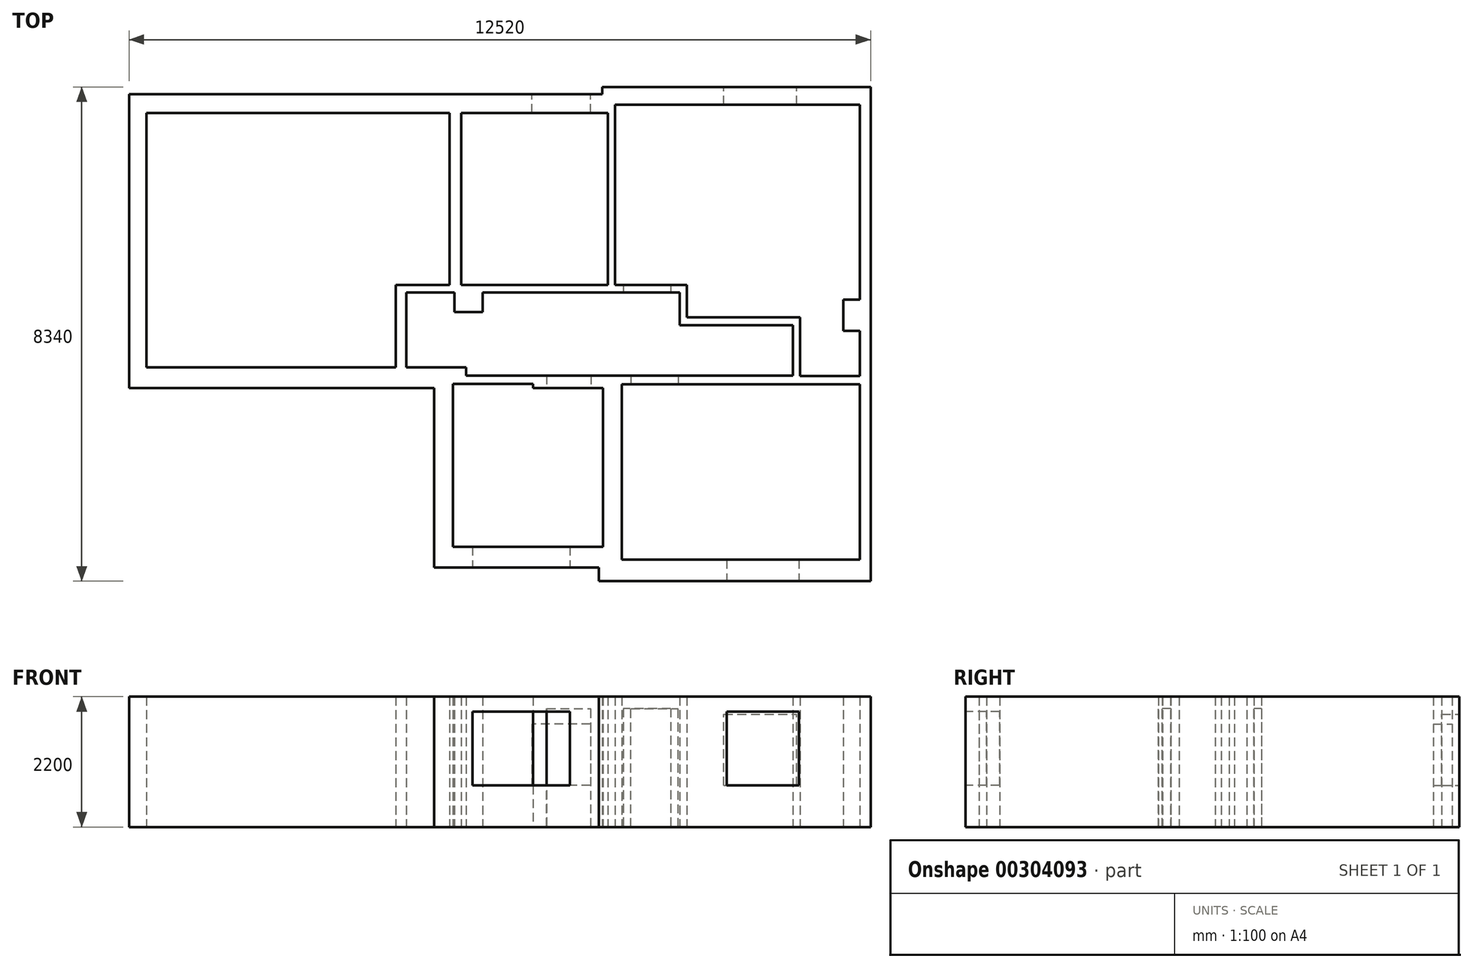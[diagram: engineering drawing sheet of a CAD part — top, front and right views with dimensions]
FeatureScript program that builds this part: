
annotation { "Feature Type Name" : "Feature", "Feature Type Description" : "" }
export const myFeature = defineFeature(function(context is Context, id is Id, definition is map)
    precondition{}
    {
        {
            var Q0;
            Q0=qCreatedBy(makeId("Top.planeOp"),FACE);
            var sketch = newSketch(context, id + "F0", { "sketchPlane" : qUnion([Q0])});
            skLineSegment(sketch, "E0", {"start": v(1913.2, -215.96) * mm, "end": v(-3236.8, -215.96) * mm});
            skLineSegment(sketch, "E1", {"start": v(-3236.8, 4744.04) * mm, "end": v(-3236.8, -215.96) * mm});
            skLineSegment(sketch, "E2", {"start": v(1913.2, -3245.96) * mm, "end": v(4693.2, -3245.96) * mm});
            skLineSegment(sketch, "E3", {"start": v(4763.2, -2895.96) * mm, "end": v(2233.2, -2895.96) * mm});
            skLineSegment(sketch, "E4", {"start": v(4693.2, -3245.96) * mm, "end": v(4693.2, -3475.96) * mm});
            skLineSegment(sketch, "E5", {"start": v(4693.2, -3475.96) * mm, "end": v(9283.2, -3475.96) * mm});
            skLineSegment(sketch, "E6", {"start": v(9283.2, -3475.96) * mm, "end": v(9283.2, 4864.04) * mm});
            skLineSegment(sketch, "E7", {"start": v(9283.2, 4864.04) * mm, "end": v(4753.2, 4864.04) * mm});
            skLineSegment(sketch, "E8", {"start": v(4968.2, 4564.04) * mm, "end": v(9103.2, 4564.04) * mm});
            skLineSegment(sketch, "E9", {"start": v(9103.2, -3115.96) * mm, "end": v(5083.2, -3115.96) * mm});
            skLineSegment(sketch, "E10", {"start": v(9103.2, -155.96) * mm, "end": v(5083.2, -155.96) * mm});
            skLineSegment(sketch, "E11.bottom", {"start": v(9103.2, 1274.04) * mm, "end": v(8823.2, 1274.04) * mm});
            skLineSegment(sketch, "E11.top", {"start": v(9103.2, 744.04) * mm, "end": v(8823.2, 744.04) * mm});
            skLineSegment(sketch, "E11.right", {"start": v(8823.2, 1274.04) * mm, "end": v(8823.2, 744.04) * mm});
            skLineSegment(sketch, "E12", {"start": v(2173.2, 4424.04) * mm, "end": v(2173.2, 1524.04) * mm});
            skLineSegment(sketch, "E13", {"start": v(2173.2, 1524.04) * mm, "end": v(1263.2, 1524.04) * mm});
            skLineSegment(sketch, "E14", {"start": v(6058.2, 1394.04) * mm, "end": v(6058.2, 844.04) * mm});
            skLineSegment(sketch, "E15", {"start": v(6058.2, 844.04) * mm, "end": v(7968.2, 844.04) * mm});
            skLineSegment(sketch, "E16", {"start": v(7968.2, 844.04) * mm, "end": v(7968.2, -5.96) * mm});
            skLineSegment(sketch, "E17", {"start": v(8088.2, -15.96) * mm, "end": v(8088.2, 974.04) * mm});
            skLineSegment(sketch, "E18", {"start": v(8088.2, 974.04) * mm, "end": v(6178.2, 974.04) * mm});
            skLineSegment(sketch, "E19", {"start": v(6178.2, 974.04) * mm, "end": v(6178.2, 1524.04) * mm});
            skLineSegment(sketch, "E20", {"start": v(6178.2, 1524.04) * mm, "end": v(4968.2, 1524.04) * mm});
            skLineSegment(sketch, "E21", {"start": v(4968.2, 1524.04) * mm, "end": v(4968.2, 4564.04) * mm});
            skLineSegment(sketch, "E22", {"start": v(4848.2, 1524.04) * mm, "end": v(2368.2, 1524.04) * mm});
            skLineSegment(sketch, "E23", {"start": v(2368.2, 1524.04) * mm, "end": v(2368.2, 4424.04) * mm});
            skLineSegment(sketch, "E24", {"start": v(2253.2, 1394.04) * mm, "end": v(2253.2, 1064.04) * mm});
            skLineSegment(sketch, "E25", {"start": v(2253.2, 1064.04) * mm, "end": v(2733.2, 1064.04) * mm});
            skLineSegment(sketch, "E26", {"start": v(2733.2, 1064.04) * mm, "end": v(2733.2, 1394.04) * mm});
            skLineSegment(sketch, "E27", {"start": v(4848.2, 4424.04) * mm, "end": v(4848.2, 1524.04) * mm});
            skLineSegment(sketch, "E28", {"start": v(4848.2, 4424.04) * mm, "end": v(2368.2, 4424.04) * mm});
            skLineSegment(sketch, "E29", {"start": v(2173.2, 4424.04) * mm, "end": v(-2946.8, 4424.04) * mm});
            skLineSegment(sketch, "E30", {"start": v(-2946.8, 4424.04) * mm, "end": v(-2946.8, 134.04) * mm});
            skLineSegment(sketch, "E31", {"start": v(1913.2, -215.96) * mm, "end": v(1913.2, -3245.96) * mm});
            skLineSegment(sketch, "E32", {"start": v(4763.2, -215.96) * mm, "end": v(4763.2, -2895.96) * mm});
            skLineSegment(sketch, "E33", {"start": v(5083.2, -155.96) * mm, "end": v(5083.2, -3115.96) * mm});
            skLineSegment(sketch, "E34", {"start": v(9103.2, -155.96) * mm, "end": v(9103.2, -3115.96) * mm});
            skLineSegment(sketch, "E35", {"start": v(9103.2, -15.96) * mm, "end": v(9103.2, 744.04) * mm});
            skLineSegment(sketch, "E36", {"start": v(9103.2, 1274.04) * mm, "end": v(9103.2, 4564.04) * mm});
            skLineSegment(sketch, "E37", {"start": v(8088.2, -15.96) * mm, "end": v(9103.2, -15.96) * mm});
            skLineSegment(sketch, "E38", {"start": v(1443.2, 1394.04) * mm, "end": v(2253.2, 1394.04) * mm});
            skLineSegment(sketch, "E39", {"start": v(2733.2, 1394.04) * mm, "end": v(6058.2, 1394.04) * mm});
            skLineSegment(sketch, "E40", {"start": v(4763.2, -215.96) * mm, "end": v(3583.2, -215.96) * mm});
            skLineSegment(sketch, "E41", {"start": v(7968.2, -5.96) * mm, "end": v(2453.2, -5.96) * mm});
            skLineSegment(sketch, "E42", {"start": v(3583.2, -215.96) * mm, "end": v(3583.2, -145.96) * mm});
            skLineSegment(sketch, "E43", {"start": v(3583.2, -145.96) * mm, "end": v(2233.2, -145.96) * mm});
            skLineSegment(sketch, "E44", {"start": v(2233.2, -145.96) * mm, "end": v(2233.2, -2895.96) * mm});
            skLineSegment(sketch, "E45", {"start": v(2453.2, -5.96) * mm, "end": v(2453.2, 134.04) * mm});
            skLineSegment(sketch, "E46", {"start": v(2453.2, 134.04) * mm, "end": v(1443.2, 134.04) * mm});
            skLineSegment(sketch, "E47", {"start": v(1443.2, 134.04) * mm, "end": v(1443.2, 1394.04) * mm});
            skLineSegment(sketch, "E48", {"start": v(1263.2, 1524.04) * mm, "end": v(1263.2, 134.04) * mm});
            skLineSegment(sketch, "E49", {"start": v(1263.2, 134.04) * mm, "end": v(-2946.8, 134.04) * mm});
            skLineSegment(sketch, "E50", {"start": v(4753.2, 4864.04) * mm, "end": v(4753.2, 4744.04) * mm});
            skLineSegment(sketch, "E51", {"start": v(4753.2, 4744.04) * mm, "end": v(-3236.8, 4744.04) * mm});
            skSolve(sketch);
        }
        {
            var Q0;
            Q0=makeQuery(id+"F0.imprint","IMPRINT",FACE,{"disambiguationData":[TD([[makeQuery(id+"F0.imprint","IMPRINT",EDGE,{"derivedFrom":sQuery(id+"F0.wireOp",EDGE,"E0")}),-1.0]])]});
            extrude(context, id + "F1", {"entities" : qUnion([Q0]), "depth" : 2200 * mm});
        }
        {
            var Q0;
            Q0=makeQuery(id+"F1.opExtrude","SWEPT_FACE",FACE,{"disambiguationData":[OSD([sQuery(id+"F0.wireOp",EDGE,"E39")])]});
            var sketch = newSketch(context, id + "F2", { "sketchPlane" : qUnion([Q0])});
            skLineSegment(sketch, "E52.bottom", {"start": v(5108.2, 0) * mm, "end": v(5908.2, 0) * mm});
            skLineSegment(sketch, "E52.top", {"start": v(5108.2, 2000) * mm, "end": v(5908.2, 2000) * mm});
            skLineSegment(sketch, "E52.left", {"start": v(5108.2, 0) * mm, "end": v(5108.2, 2000) * mm});
            skLineSegment(sketch, "E52.right", {"start": v(5908.2, 0) * mm, "end": v(5908.2, 2000) * mm});
            skSolve(sketch);
        }
        {
            var Q0;
            Q0=makeQuery(id+"F2.imprint","IMPRINT",FACE,{"disambiguationData":[TD([[makeQuery(id+"F2.imprint","IMPRINT",EDGE,{"derivedFrom":sQuery(id+"F2.wireOp",EDGE,"E52.bottom")}),1.0]])]});
            extrude(context, id + "F3", {"entities" : qUnion([Q0]), "operationType" : NewBodyOperationType.REMOVE, "endBound" : BoundingType.UP_TO_NEXT, "oppositeDirection" : true, "depth" : 25 * mm});
        }
        {
            var Q0;
            Q0=makeQuery(id+"F1.opExtrude","SWEPT_FACE",FACE,{"disambiguationData":[OSD([sQuery(id+"F0.wireOp",EDGE,"E10")])]});
            var sketch = newSketch(context, id + "F4", { "sketchPlane" : qUnion([Q0])});
            skLineSegment(sketch, "E53.bottom", {"start": v(5233.2, 0) * mm, "end": v(6033.2, 0) * mm});
            skLineSegment(sketch, "E53.top", {"start": v(5233.2, 2000) * mm, "end": v(6033.2, 2000) * mm});
            skLineSegment(sketch, "E53.left", {"start": v(5233.2, 0) * mm, "end": v(5233.2, 2000) * mm});
            skLineSegment(sketch, "E53.right", {"start": v(6033.2, 0) * mm, "end": v(6033.2, 2000) * mm});
            skSolve(sketch);
        }
        {
            var Q0;
            Q0=makeQuery(id+"F4.imprint","IMPRINT",FACE,{"disambiguationData":[TD([[makeQuery(id+"F4.imprint","IMPRINT",EDGE,{"derivedFrom":sQuery(id+"F4.wireOp",EDGE,"E53.bottom")}),-1.0]])]});
            extrude(context, id + "F5", {"entities" : qUnion([Q0]), "operationType" : NewBodyOperationType.REMOVE, "endBound" : BoundingType.UP_TO_NEXT, "oppositeDirection" : true, "depth" : 25 * mm});
        }
        {
            var Q0;
            Q0=makeQuery(id+"F1.opExtrude","SWEPT_FACE",FACE,{"disambiguationData":[OSD([sQuery(id+"F0.wireOp",EDGE,"E2")])]});
            var sketch = newSketch(context, id + "F6", { "sketchPlane" : qUnion([Q0])});
            skLineSegment(sketch, "E54.bottom", {"start": v(2563.2, 1950) * mm, "end": v(4203.2, 1950) * mm});
            skLineSegment(sketch, "E54.top", {"start": v(2563.2, 700) * mm, "end": v(4203.2, 700) * mm});
            skLineSegment(sketch, "E54.left", {"start": v(2563.2, 1950) * mm, "end": v(2563.2, 700) * mm});
            skLineSegment(sketch, "E54.right", {"start": v(4203.2, 1950) * mm, "end": v(4203.2, 700) * mm});
            skSolve(sketch);
        }
        {
            var Q0;
            Q0=makeQuery(id+"F6.imprint","IMPRINT",FACE,{"disambiguationData":[TD([[makeQuery(id+"F6.imprint","IMPRINT",EDGE,{"derivedFrom":sQuery(id+"F6.wireOp",EDGE,"E54.bottom")}),-1.0]])]});
            extrude(context, id + "F7", {"entities" : qUnion([Q0]), "operationType" : NewBodyOperationType.REMOVE, "endBound" : BoundingType.UP_TO_NEXT, "oppositeDirection" : true, "depth" : 25 * mm});
        }
        {
            var Q0;
            Q0=makeQuery(id+"F1.opExtrude","SWEPT_FACE",FACE,{"disambiguationData":[OSD([sQuery(id+"F0.wireOp",EDGE,"E5")])]});
            var sketch = newSketch(context, id + "F8", { "sketchPlane" : qUnion([Q0])});
            skLineSegment(sketch, "E55.bottom", {"start": v(6853.2, 1950) * mm, "end": v(8073.2, 1950) * mm});
            skLineSegment(sketch, "E55.top", {"start": v(6853.2, 700) * mm, "end": v(8073.2, 700) * mm});
            skLineSegment(sketch, "E55.left", {"start": v(6853.2, 1950) * mm, "end": v(6853.2, 700) * mm});
            skLineSegment(sketch, "E55.right", {"start": v(8073.2, 1950) * mm, "end": v(8073.2, 700) * mm});
            skSolve(sketch);
        }
        {
            var Q0;
            Q0=makeQuery(id+"F8.imprint","IMPRINT",FACE,{"disambiguationData":[TD([[makeQuery(id+"F8.imprint","IMPRINT",EDGE,{"derivedFrom":sQuery(id+"F8.wireOp",EDGE,"E55.bottom")}),-1.0]])]});
            extrude(context, id + "F9", {"entities" : qUnion([Q0]), "operationType" : NewBodyOperationType.REMOVE, "endBound" : BoundingType.UP_TO_NEXT, "oppositeDirection" : true, "depth" : 25 * mm});
        }
        {
            var Q0;
            Q0=makeQuery(id+"F1.opExtrude","SWEPT_FACE",FACE,{"disambiguationData":[OSD([sQuery(id+"F0.wireOp",EDGE,"E51")])]});
            var sketch = newSketch(context, id + "F10", { "sketchPlane" : qUnion([Q0])});
            skLineSegment(sketch, "E56.bottom", {"start": v(-4553.2, 1740) * mm, "end": v(-3563.2, 1740) * mm});
            skLineSegment(sketch, "E56.top", {"start": v(-4553.2, 700) * mm, "end": v(-3563.2, 700) * mm});
            skLineSegment(sketch, "E56.left", {"start": v(-4553.2, 1740) * mm, "end": v(-4553.2, 700) * mm});
            skLineSegment(sketch, "E56.right", {"start": v(-3563.2, 1740) * mm, "end": v(-3563.2, 700) * mm});
            skSolve(sketch);
        }
        {
            var Q0;
            Q0=makeQuery(id+"F10.imprint","IMPRINT",FACE,{"disambiguationData":[TD([[makeQuery(id+"F10.imprint","IMPRINT",EDGE,{"derivedFrom":sQuery(id+"F10.wireOp",EDGE,"E56.bottom")}),-1.0]])]});
            extrude(context, id + "F11", {"entities" : qUnion([Q0]), "operationType" : NewBodyOperationType.REMOVE, "endBound" : BoundingType.UP_TO_NEXT, "oppositeDirection" : true, "depth" : 25 * mm});
        }
        {
            var Q0;
            Q0=makeQuery(id+"F1.opExtrude","SWEPT_FACE",FACE,{"disambiguationData":[OSD([sQuery(id+"F0.wireOp",EDGE,"E7")])]});
            var sketch = newSketch(context, id + "F12", { "sketchPlane" : qUnion([Q0])});
            skLineSegment(sketch, "E57.bottom", {"start": v(-8033.2, 1900) * mm, "end": v(-6803.2, 1900) * mm});
            skLineSegment(sketch, "E57.top", {"start": v(-8033.2, 700) * mm, "end": v(-6803.2, 700) * mm});
            skLineSegment(sketch, "E57.left", {"start": v(-8033.2, 1900) * mm, "end": v(-8033.2, 700) * mm});
            skLineSegment(sketch, "E57.right", {"start": v(-6803.2, 1900) * mm, "end": v(-6803.2, 700) * mm});
            skSolve(sketch);
        }
        {
            var Q0;
            Q0=makeQuery(id+"F12.imprint","IMPRINT",FACE,{"disambiguationData":[TD([[makeQuery(id+"F12.imprint","IMPRINT",EDGE,{"derivedFrom":sQuery(id+"F12.wireOp",EDGE,"E57.bottom")}),-1.0]])]});
            extrude(context, id + "F13", {"entities" : qUnion([Q0]), "operationType" : NewBodyOperationType.REMOVE, "endBound" : BoundingType.UP_TO_NEXT, "oppositeDirection" : true, "depth" : 25 * mm});
        }
        {
            var Q0;
            Q0=makeQuery(id+"F1.opExtrude","SWEPT_FACE",FACE,{"disambiguationData":[OSD([sQuery(id+"F0.wireOp",EDGE,"E40")])]});
            var sketch = newSketch(context, id + "F14", { "sketchPlane" : qUnion([Q0])});
            skLineSegment(sketch, "E58.bottom", {"start": v(3813.2, 0) * mm, "end": v(4563.2, 0) * mm});
            skLineSegment(sketch, "E58.top", {"start": v(3813.2, 2000) * mm, "end": v(4563.2, 2000) * mm});
            skLineSegment(sketch, "E58.left", {"start": v(3813.2, 0) * mm, "end": v(3813.2, 2000) * mm});
            skLineSegment(sketch, "E58.right", {"start": v(4563.2, 0) * mm, "end": v(4563.2, 2000) * mm});
            skSolve(sketch);
        }
        {
            var Q0;
            Q0=makeQuery(id+"F14.imprint","IMPRINT",FACE,{"disambiguationData":[TD([[makeQuery(id+"F14.imprint","IMPRINT",EDGE,{"derivedFrom":sQuery(id+"F14.wireOp",EDGE,"E58.bottom")}),-1.0]])]});
            extrude(context, id + "F15", {"entities" : qUnion([Q0]), "operationType" : NewBodyOperationType.REMOVE, "endBound" : BoundingType.UP_TO_NEXT, "oppositeDirection" : true, "depth" : 25 * mm});
        }
    });
